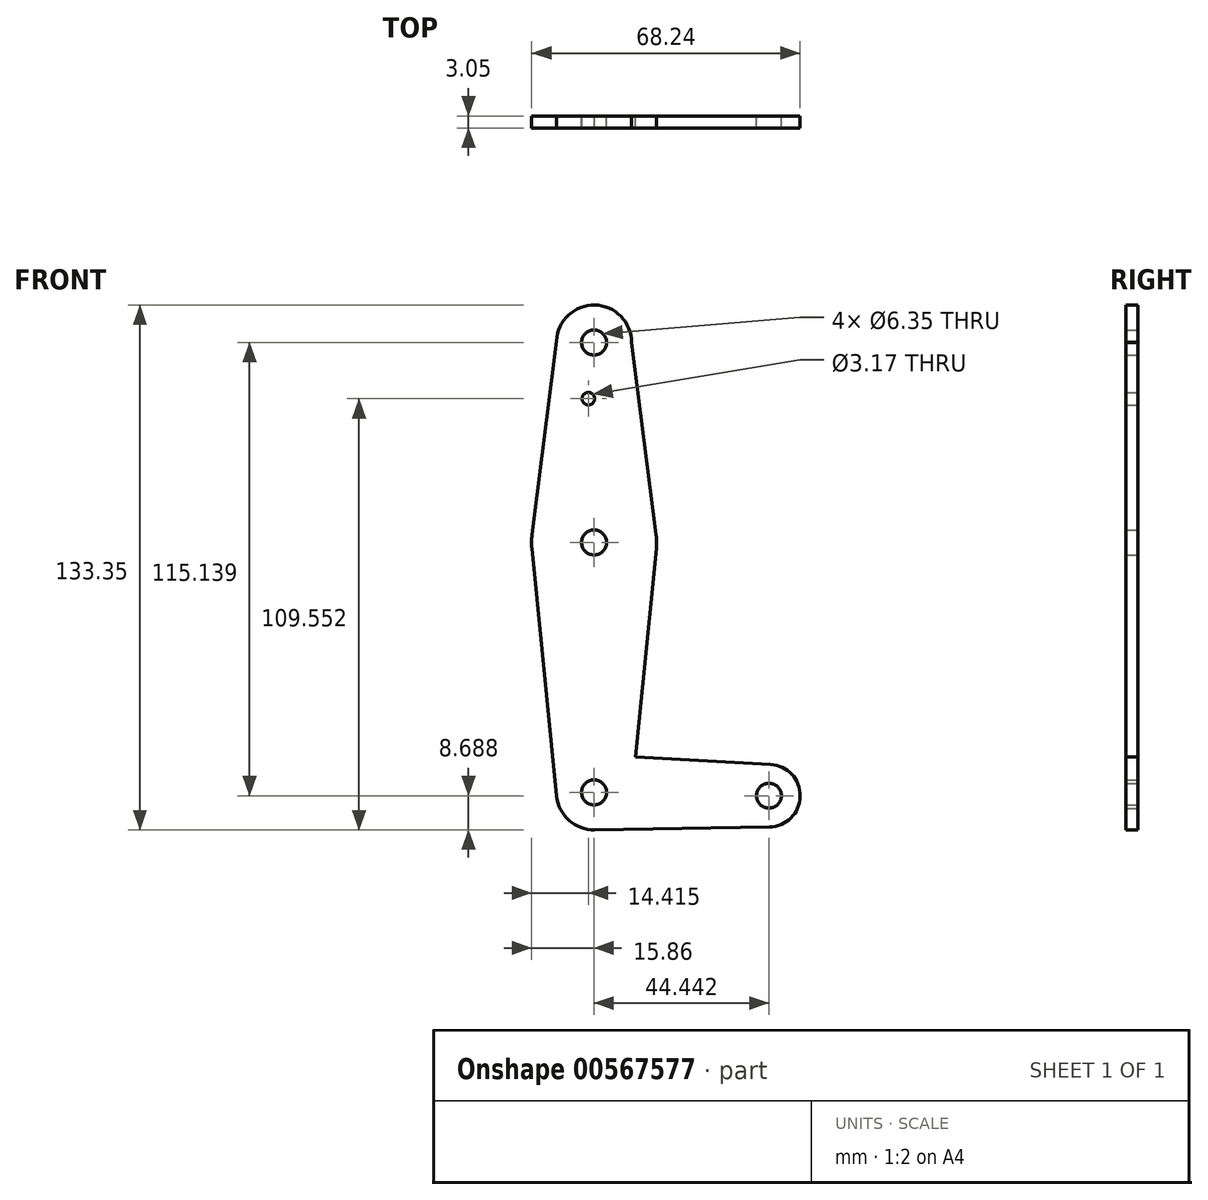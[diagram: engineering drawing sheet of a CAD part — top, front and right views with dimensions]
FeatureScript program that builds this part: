
annotation { "Feature Type Name" : "Feature", "Feature Type Description" : "" }
export const myFeature = defineFeature(function(context is Context, id is Id, definition is map)
    precondition{}
    {
        {
            var Q0;
            Q0=qCreatedBy(makeId("Front.planeOp"),FACE);
            var sketch = newSketch(context, id + "F0", { "sketchPlane" : qUnion([Q0])});
            skCircle(sketch, "E0", {"center": v(0, 76.33) * mm, "radius": 9.53 * mm});
            skCircle(sketch, "E1", {"center": v(0, -37.97) * mm, "radius": 9.53 * mm});
            skCircle(sketch, "E2", {"center": v(44.44, -38.81) * mm, "radius": 7.94 * mm});
            skCircle(sketch, "E3", {"center": v(0.02, 25.53) * mm, "radius": 15.88 * mm});
            skLineSegment(sketch, "E4", {"start": v(-9.52, 76.72) * mm, "end": v(-15.73, 27.52) * mm});
            skLineSegment(sketch, "E5", {"start": v(9.53, 76.33) * mm, "end": v(15.76, 27.54) * mm});
            skCircle(sketch, "E6", {"center": v(0.02, 25.53) * mm, "radius": 3.18 * mm});
            skCircle(sketch, "E7", {"center": v(0, 76.33) * mm, "radius": 3.18 * mm});
            skCircle(sketch, "E8", {"center": v(0, -37.97) * mm, "radius": 3.17 * mm});
            skCircle(sketch, "E9", {"center": v(44.44, -38.81) * mm, "radius": 3.17 * mm});
            skCircle(sketch, "E10", {"center": v(-1.44, 62.05) * mm, "radius": 1.59 * mm});
            skLineSegment(sketch, "E11", {"start": v(0.52, -28.46) * mm, "end": v(44.88, -30.89) * mm});
            skLineSegment(sketch, "E12", {"start": v(0.16, -47.5) * mm, "end": v(44.58, -46.75) * mm});
            skLineSegment(sketch, "E13", {"start": v(0, 76.33) * mm, "end": v(0, -37.97) * mm, "construction": true});
            skLineSegment(sketch, "E14", {"start": v(-15.78, 23.94) * mm, "end": v(-9.48, -38.92) * mm});
            skLineSegment(sketch, "E15", {"start": v(15.81, 23.94) * mm, "end": v(9.48, -38.93) * mm});
            skLineSegment(sketch, "E16", {"start": v(0, -37.97) * mm, "end": v(44.44, -38.81) * mm, "construction": true});
            skSolve(sketch);
        }
        {
            var Q0;
            Q0 = qSketchRegion(id + "F0", true);
            extrude(context, id + "F1", {"entities" : qUnion([Q0]), "depth" : 3.05 * mm, "offsetDistance" : 25.4 * mm});
        }
    });
